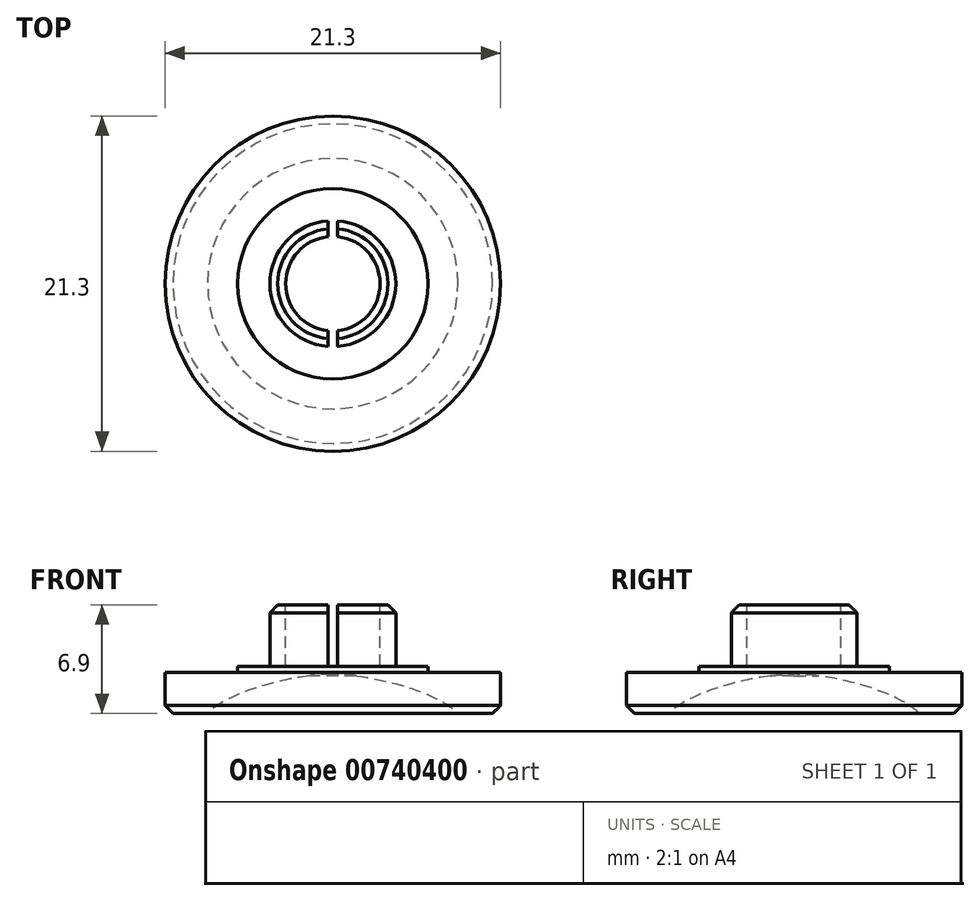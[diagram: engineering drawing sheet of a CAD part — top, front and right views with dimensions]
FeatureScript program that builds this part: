
annotation { "Feature Type Name" : "Feature", "Feature Type Description" : "" }
export const myFeature = defineFeature(function(context is Context, id is Id, definition is map)
    precondition{}
    {
        {
            var Q0;
            Q0=qCreatedBy(makeId("Front.planeOp"),FACE);
            var sketch = newSketch(context, id + "F0", { "sketchPlane" : qUnion([Q0])});
            skLineSegment(sketch, "E0", {"start": v(0, 0) * mm, "end": v(7.95, 0) * mm});
            skLineSegment(sketch, "E1", {"start": v(7.95, 0) * mm, "end": v(10.65, 0) * mm});
            skLineSegment(sketch, "E2", {"start": v(10.65, 0) * mm, "end": v(10.65, 2.6) * mm});
            skLineSegment(sketch, "E3", {"start": v(10.65, 2.6) * mm, "end": v(6.05, 2.6) * mm});
            skLineSegment(sketch, "E4", {"start": v(6.05, 2.6) * mm, "end": v(6.05, 3) * mm});
            skLineSegment(sketch, "E5", {"start": v(6.05, 3) * mm, "end": v(4, 3) * mm});
            skLineSegment(sketch, "E6", {"start": v(4, 3) * mm, "end": v(4, 6.9) * mm});
            skLineSegment(sketch, "E7", {"start": v(4, 6.9) * mm, "end": v(0, 6.9) * mm});
            skLineSegment(sketch, "E8", {"start": v(0, 6.9) * mm, "end": v(0, 0) * mm});
            skLineSegment(sketch, "E9", {"start": v(0, 0) * mm, "end": v(0, 2.5) * mm});
            skFitSpline(sketch, "E10", {"points": [v(0, 2.5) * mm, v(7.95, 0) * mm], "startDerivative": vector(7.15, -0.05) * mm, "endDerivative": vector(4.23, -4.42) * mm});
            skLineSegment(sketch, "E11", {"start": v(0, 2.89) * mm, "end": v(1.5, 2.89) * mm});
            skLineSegment(sketch, "E12", {"start": v(1.5, 2.89) * mm, "end": v(1.5, 2.39) * mm});
            skSolve(sketch);
        }
        {
            var Q0;
            Q0=makeQuery(id+"F0.imprint","IMPRINT",FACE,{"disambiguationData":[TD([[makeQuery(id+"F0.imprint","IMPRINT",EDGE,{"derivedFrom":sQuery(id+"F0.wireOp",EDGE,"E1")}),1.0]])]});
            var Q1;
            {var subQ3=sQuery(id+"F0.wireOp",EDGE,"E11");Q1=makeQuery(id+"F0.imprint","IMPRINT",FACE,{"disambiguationData":[TD([[makeQuery(id+"F0.imprint","IMPRINT",EDGE,{"derivedFrom":subQ3}),-1.0]])]});}
            var Q2;
            Q2=sQuery(id+"F0.wireOp",EDGE,"E8");
            revolve(context, id + "F1", {"surfaceOperationType" : NewSurfaceOperationType.NEW, "entities" : qUnion([Q0, Q1]), "axis" : qUnion([Q2]), "revolveType" : RevolveType.FULL});
        }
        {
            var Q0;
            Q0=makeQuery(id+"F1.opRevolve","SWEPT_EDGE",EDGE,{"disambiguationData":[OSD([sQuery(id+"F0.wireOp",EDGE,"E6"),sQuery(id+"F0.wireOp",EDGE,"E7")])]});
            chamfer(context, id + "F2", {"entities" : qUnion([Q0]), "width" : .5 * mm, "tangentPropagation" : true});
        }
        {
            var Q0;
            Q0=makeQuery(id+"F1.opRevolve","SWEPT_EDGE",EDGE,{"disambiguationData":[OSD([sQuery(id+"F0.wireOp",EDGE,"E1"),sQuery(id+"F0.wireOp",EDGE,"E2")])]});
            chamfer(context, id + "F3", {"entities" : qUnion([Q0]), "width" : .5 * mm, "tangentPropagation" : true});
        }
        {
            var Q0;
            Q0=qCreatedBy(makeId("Top.planeOp"),FACE);
            cPlane(context, id + "F4", {"entities" : qUnion([Q0]), "cplaneType" : CPlaneType.OFFSET, "offset" : 6.9 * mm, "width" : 150 * mm, "height" : 150 * mm});
        }
        {
            var Q0;
            Q0=qCreatedBy(id+"F4.planeOp",FACE);
            var sketch = newSketch(context, id + "F5", { "sketchPlane" : qUnion([Q0])});
            skCircle(sketch, "E13", {"center": v(0, 0) * mm, "radius": 3 * mm});
            skLineSegment(sketch, "E14", {"start": v(0, 0) * mm, "end": v(0.3, 0) * mm});
            skLineSegment(sketch, "E15", {"start": v(0, 0) * mm, "end": v(-0.3, 0) * mm});
            skLineSegment(sketch, "E16", {"start": v(0.3, 0) * mm, "end": v(0.3, -4.24) * mm});
            skLineSegment(sketch, "E17", {"start": v(0.3, 0) * mm, "end": v(0.3, 4.03) * mm});
            skLineSegment(sketch, "E18.bottom", {"start": v(-0.3, 0) * mm, "end": v(0.3, 0) * mm});
            skLineSegment(sketch, "E18.top", {"start": v(-0.3, 4.03) * mm, "end": v(0.3, 4.03) * mm});
            skLineSegment(sketch, "E18.left", {"start": v(-0.3, 0) * mm, "end": v(-0.3, 4.03) * mm});
            skLineSegment(sketch, "E19.top", {"start": v(-0.3, -4.24) * mm, "end": v(0.3, -4.24) * mm});
            skLineSegment(sketch, "E19.left", {"start": v(-0.3, 0) * mm, "end": v(-0.3, -4.24) * mm});
            skSolve(sketch);
        }
        {
            var Q0;
            Q0=qSketchRegion(id+"F5",true);
            extrude(context, id + "F6", {"entities" : qUnion([Q0]), "operationType" : NewBodyOperationType.REMOVE, "oppositeDirection" : true, "depth" : 3.9 * mm, "offsetDistance" : 25 * mm});
        }
    });
